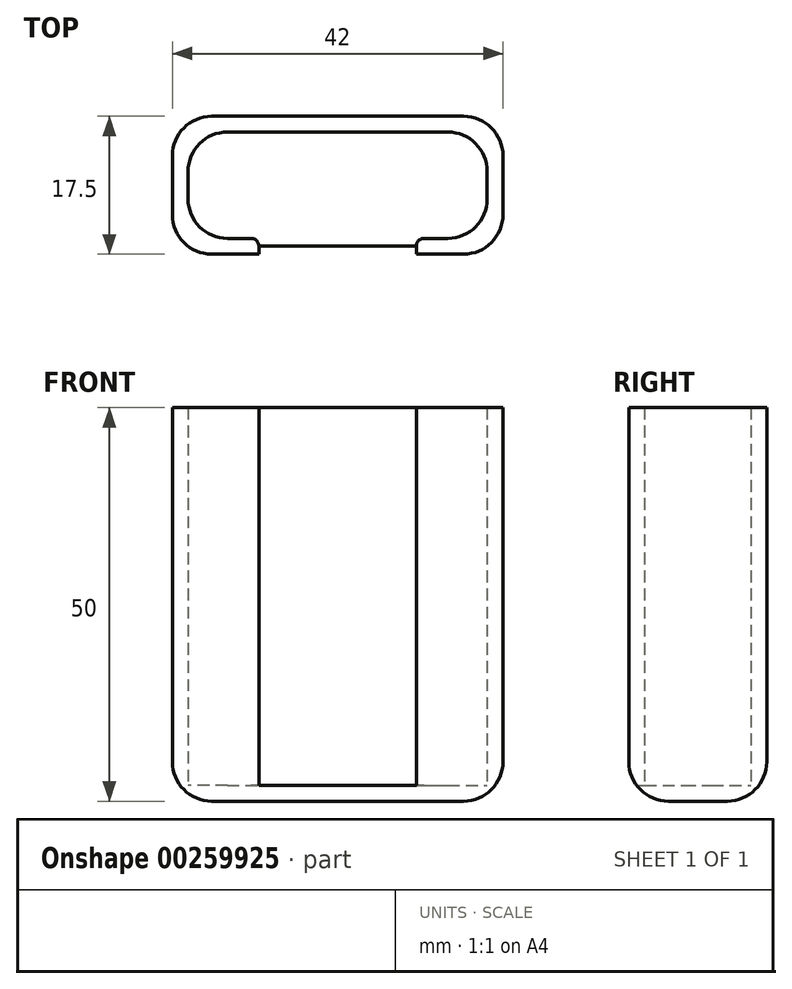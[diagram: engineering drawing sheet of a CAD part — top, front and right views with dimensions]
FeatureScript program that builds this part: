
annotation { "Feature Type Name" : "Feature", "Feature Type Description" : "" }
export const myFeature = defineFeature(function(context is Context, id is Id, definition is map)
    precondition{}
    {
        {
            var Q0;
            Q0=qCreatedBy(makeId("Top.planeOp"),FACE);
            var sketch = newSketch(context, id + "F0", { "sketchPlane" : qUnion([Q0])});
            skLineSegment(sketch, "E0.bottom", {"start": v(-9, 0) * mm, "end": v(29, 0) * mm});
            skLineSegment(sketch, "E0.top", {"start": v(-9, 13.5) * mm, "end": v(29, 13.5) * mm});
            skLineSegment(sketch, "E0.left", {"start": v(-9, 0) * mm, "end": v(-9, 13.5) * mm});
            skLineSegment(sketch, "E0.right", {"start": v(29, 0) * mm, "end": v(29, 13.5) * mm});
            skLineSegment(sketch, "E1.0", {"start": v(-11, -2) * mm, "end": v(31, -2) * mm});
            skLineSegment(sketch, "E1.1", {"start": v(-11, -2) * mm, "end": v(-11, 15.5) * mm});
            skLineSegment(sketch, "E1.2", {"start": v(-11, 15.5) * mm, "end": v(31, 15.5) * mm});
            skLineSegment(sketch, "E1.3", {"start": v(31, -2) * mm, "end": v(31, 15.5) * mm});
            skLineSegment(sketch, "E2", {"start": v(20, -2) * mm, "end": v(20, 0) * mm});
            skLineSegment(sketch, "E3", {"start": v(20, 0) * mm, "end": v(0, 0) * mm});
            skLineSegment(sketch, "E4", {"start": v(0, 0) * mm, "end": v(0, -2) * mm});
            skLineSegment(sketch, "E5", {"start": v(0, -2) * mm, "end": v(20, -2) * mm});
            skSolve(sketch);
        }
        {
            var Q0;
            Q0=makeQuery(id+"F0.imprint","IMPRINT",FACE,{"disambiguationData":[TD([[makeQuery(id+"F0.imprint","IMPRINT",EDGE,{"derivedFrom":sQuery(id+"F0.wireOp",EDGE,"E0.top")}),1.0]])]});
            extrude(context, id + "F1", {"entities" : qUnion([Q0]), "depth" : 50 * mm});
        }
        {
            var Q0;
            Q0=makeQuery(id+"F0.imprint","IMPRINT",FACE,{"disambiguationData":[TD([[makeQuery(id+"F0.imprint","IMPRINT",EDGE,{"derivedFrom":sQuery(id+"F0.wireOp",EDGE,"E0.top")}),-1.0]])]});
            var Q1;
            Q1=makeQuery(id+"F0.imprint","IMPRINT",FACE,{"disambiguationData":[TD([[makeQuery(id+"F0.imprint","IMPRINT",EDGE,{"derivedFrom":sQuery(id+"F0.wireOp",EDGE,"E2")}),1.0]])]});
            extrude(context, id + "F2", {"entities" : qUnion([Q0, Q1]), "operationType" : NewBodyOperationType.ADD, "depth" : 2 * mm});
        }
        {
            var Q0;
            Q0=makeQuery(id+"F1.opExtrude","SWEPT_EDGE",EDGE,{"disambiguationData":[OSD([sQuery(id+"F0.wireOp",EDGE,"E0.bottom"),sQuery(id+"F0.wireOp",EDGE,"E0.right")])]});
            var Q1;
            Q1=makeQuery(id+"F1.opExtrude","SWEPT_EDGE",EDGE,{"disambiguationData":[OSD([sQuery(id+"F0.wireOp",EDGE,"E0.top"),sQuery(id+"F0.wireOp",EDGE,"E0.right")])]});
            var Q2;
            Q2=makeQuery(id+"F1.opExtrude","SWEPT_EDGE",EDGE,{"disambiguationData":[OSD([sQuery(id+"F0.wireOp",EDGE,"E0.bottom"),sQuery(id+"F0.wireOp",EDGE,"E0.left")])]});
            var Q3;
            Q3=makeQuery(id+"F1.opExtrude","SWEPT_EDGE",EDGE,{"disambiguationData":[OSD([sQuery(id+"F0.wireOp",EDGE,"E0.top"),sQuery(id+"F0.wireOp",EDGE,"E0.left")])]});
            var Q4;
            Q4=makeQuery(id+"F1.opExtrude","SWEPT_EDGE",EDGE,{"disambiguationData":[OSD([sQuery(id+"F0.wireOp",EDGE,"E1.1"),sQuery(id+"F0.wireOp",EDGE,"E1.2")])]});
            var Q5;
            Q5=makeQuery(id+"F1.opExtrude","SWEPT_EDGE",EDGE,{"disambiguationData":[OSD([sQuery(id+"F0.wireOp",EDGE,"E1.0"),sQuery(id+"F0.wireOp",EDGE,"E1.1")])]});
            var Q6;
            Q6=makeQuery(id+"F1.opExtrude","SWEPT_EDGE",EDGE,{"disambiguationData":[OSD([sQuery(id+"F0.wireOp",EDGE,"E1.2"),sQuery(id+"F0.wireOp",EDGE,"E1.3")])]});
            var Q7;
            Q7=makeQuery(id+"F1.opExtrude","SWEPT_EDGE",EDGE,{"disambiguationData":[OSD([sQuery(id+"F0.wireOp",EDGE,"E1.0"),sQuery(id+"F0.wireOp",EDGE,"E1.3")])]});
            var Q8;
            {var subQ0=sQuery(id+"F0.wireOp",EDGE,"E5");var subQ1=sQuery(id+"F0.wireOp",EDGE,"E1.0");Q8=makeQuery(id+"F2.boolean.opBoolean","MERGE",EDGE,{"derivedFrom":[makeQuery(id+"F1.opExtrude","CAP_EDGE",EDGE,{"disambiguationData":[OSD([subQ1]),TDD([makeQuery(id+"F0.imprint","IMPRINT",EDGE,{"disambiguationData":[TD([[makeQuery(id+"F0.imprint","INTERSECT",VERTEX,{"derivedFrom":[subQ1,sQuery(id+"F0.wireOp",EDGE,"E1.1")]}),-1.0]])],"derivedFrom":subQ1})])],"isStart":true}),makeQuery(id+"F1.opExtrude","CAP_EDGE",EDGE,{"disambiguationData":[OSD([subQ1]),TDD([makeQuery(id+"F0.imprint","IMPRINT",EDGE,{"disambiguationData":[TD([[makeQuery(id+"F0.imprint","INTERSECT",VERTEX,{"derivedFrom":[subQ1,sQuery(id+"F0.wireOp",EDGE,"E1.3")]}),1.0]])],"derivedFrom":subQ1})])],"isStart":true}),makeQuery(id+"F2.opExtrude","CAP_EDGE",EDGE,{"disambiguationData":[OSD([subQ0])],"isStart":true})]});}
            var Q9;
            Q9=makeQuery(id+"F1.opExtrude","CAP_EDGE",EDGE,{"disambiguationData":[OSD([sQuery(id+"F0.wireOp",EDGE,"E1.2")])],"isStart":true});
            var Q10;
            Q10=makeQuery(id+"F1.opExtrude","CAP_EDGE",EDGE,{"disambiguationData":[OSD([sQuery(id+"F0.wireOp",EDGE,"E1.3")])],"isStart":true});
            var Q11;
            Q11=makeQuery(id+"F1.opExtrude","CAP_EDGE",EDGE,{"disambiguationData":[OSD([sQuery(id+"F0.wireOp",EDGE,"E1.1")])],"isStart":true});
            fillet(context, id + "F3", {"entities" : qUnion([Q0, Q1, Q2, Q3, Q4, Q5, Q6, Q7, Q8, Q9, Q10, Q11]), "radius" : 5 * mm, "tangentPropagation" : true, "allowEdgeOverflow" : false});
        }
        {
            var Q0;
            Q0=makeQuery(id+"F1.opExtrude","SWEPT_EDGE",EDGE,{"disambiguationData":[OSD([sQuery(id+"F0.wireOp",EDGE,"E0.bottom"),sQuery(id+"F0.wireOp",EDGE,"E3"),sQuery(id+"F0.wireOp",EDGE,"E4")])]});
            var Q1;
            Q1=makeQuery(id+"F1.opExtrude","SWEPT_EDGE",EDGE,{"disambiguationData":[OSD([sQuery(id+"F0.wireOp",EDGE,"E0.bottom"),sQuery(id+"F0.wireOp",EDGE,"E2"),sQuery(id+"F0.wireOp",EDGE,"E3")])]});
            fillet(context, id + "F4", {"entities" : qUnion([Q0, Q1]), "radius" : 1 * mm, "tangentPropagation" : true, "allowEdgeOverflow" : false});
        }
    });
